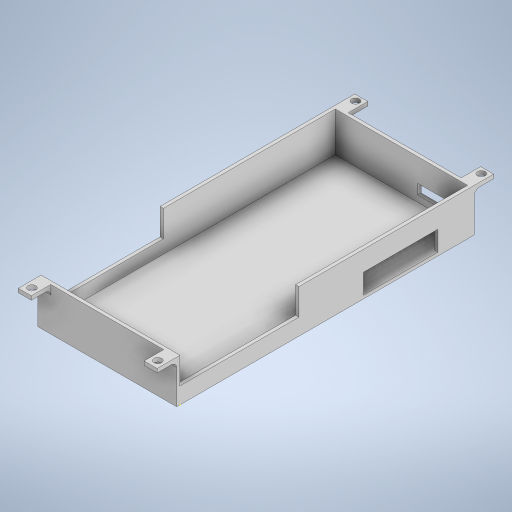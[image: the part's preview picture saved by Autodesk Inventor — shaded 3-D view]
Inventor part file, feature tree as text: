
AUTODESK INVENTOR PART (.ipt)
format: ipt  version: 2024.2 (Build 282272000, 272)  size: 366,080 bytes
history: native  units: in
note: dims shown in document units (in); Inventor stores cm internally (conversion verified against a paired STEP export)
features: sketch x10, extrude x8, fillet x1, hole x1, pattern_linear x1, projected_geometry x1
ambient origin geometry x8: Origin, YZ Plane, XZ Plane, XY Plane, X Axis, Y Axis, Z Axis, Center Point
bodies: Solid1 (feature_tree)
feature tree (22):
  extrude  "Extrusion1"  Depth=8.8in
  extrude  "Extrusion2"  Depth=0.1in
  extrude  "Extrusion3"  Depth=0.1in
  extrude  "Extrusion4"  Depth=1.3in
  extrude  "Extrusion5"  Depth=3.6in
  fillet  "Fillet1"  Radius=0.8in
  sketch  "Sketch6"  dims[d12=1.3in d13=0.0in]
  extrude  "Extrusion6"  TaperAngle=0.0deg  [1 undecoded]
  extrude  "Extrusion7"  TaperAngle=0.0deg  [1 undecoded]
  extrude  "Extrusion8"  Depth=0.3937in
  hole  "Hole1"  [1 undecoded]
  pattern_linear  "Rectangular Pattern1"  Spacing1=3.25in  [1 undecoded]
  sketch  "Sketch1"  dims[d0=4.0in d1=8.8in]
  sketch  "Sketch2"  dims[d2=0.1in d3=0.0in d4=0.1in]
  sketch  "Sketch3"  dims[d5=0.1in d6=0.1in]
  sketch  "Sketch4"  dims[d7=0.1in d8=1.3in]
  sketch  "Sketch5"  dims[d9=0.0in d10=3.6in d11=0.8in]
  sketch  "Sketch7"  dims[d14=1.5in d15=0.0in d16=0.0in]
  sketch  "Sketch8"  dims[d17=0.5in d21=0.3937in]
  projected_geometry  "Projected Loop1"
  sketch  "Sketch9"  dims[d22=0.5906in d23=0.1181in d24=0.0in]
  sketch  "Sketch10"  dims[d25=0.1575in d26=3.25in d27=0.6in d28=0.1181in d29=0.0in d30=1.0in d31=0.0in d32=0.2in d33=0.0in d34=0.2362in d35=0.75in d36=0.375in d37=0.25in d38=0.5635in d39=1.0in d40=0.0in d41=0.7874in d43=3.8063in d44=0.7874in d46=9.7873in]
note: 4 required parameter values undecoded (feature->parameter linkage not recoverable at this tier; creation-order binding heuristic only, values carry confidence <= 0.55)
